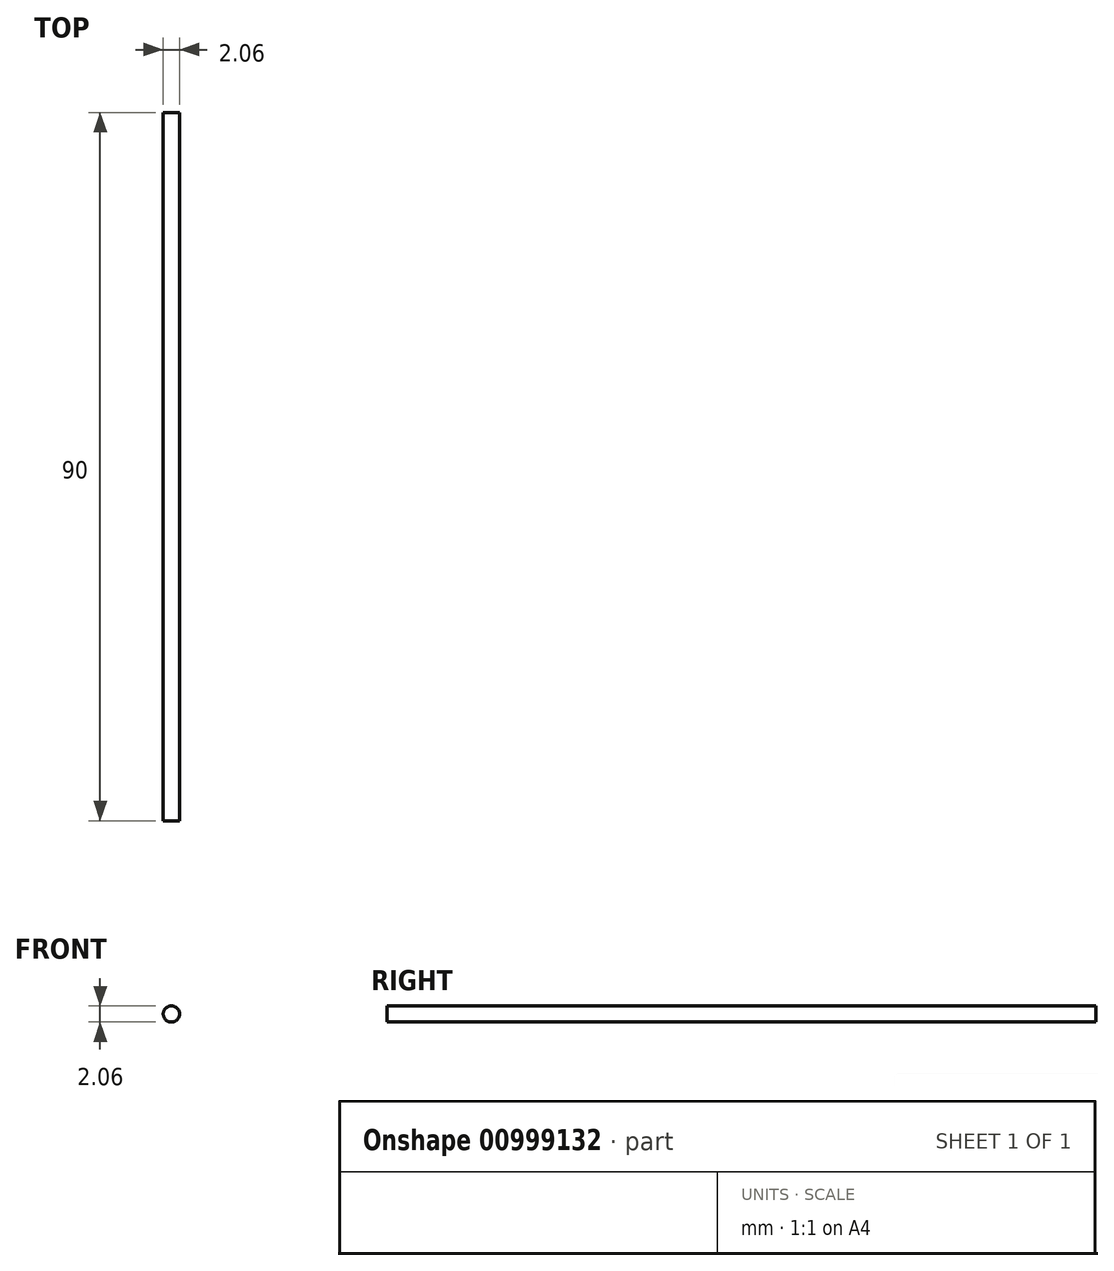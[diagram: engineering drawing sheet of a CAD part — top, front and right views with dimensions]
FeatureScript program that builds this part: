
annotation { "Feature Type Name" : "Feature", "Feature Type Description" : "" }
export const myFeature = defineFeature(function(context is Context, id is Id, definition is map)
    precondition{}
    {
        {
            var Q0;
            Q0=qCreatedBy(makeId("Front.planeOp"),FACE);
            var sketch = newSketch(context, id + "F0", { "sketchPlane" : qUnion([Q0])});
            skCircle(sketch, "E0", {"center": v(0, 0) * mm, "radius": 1.03 * mm});
            skPoint(sketch, "E1", {"position": v(1, -0.26) * mm});
            skSolve(sketch);
        }
        {
            var Q0;
            Q0 = qSketchRegion(id + "F0", true);
            extrude(context, id + "F1", {"entities" : qUnion([Q0]), "depth" : 90 * mm, "offsetDistance" : 25 * mm});
        }
    });
